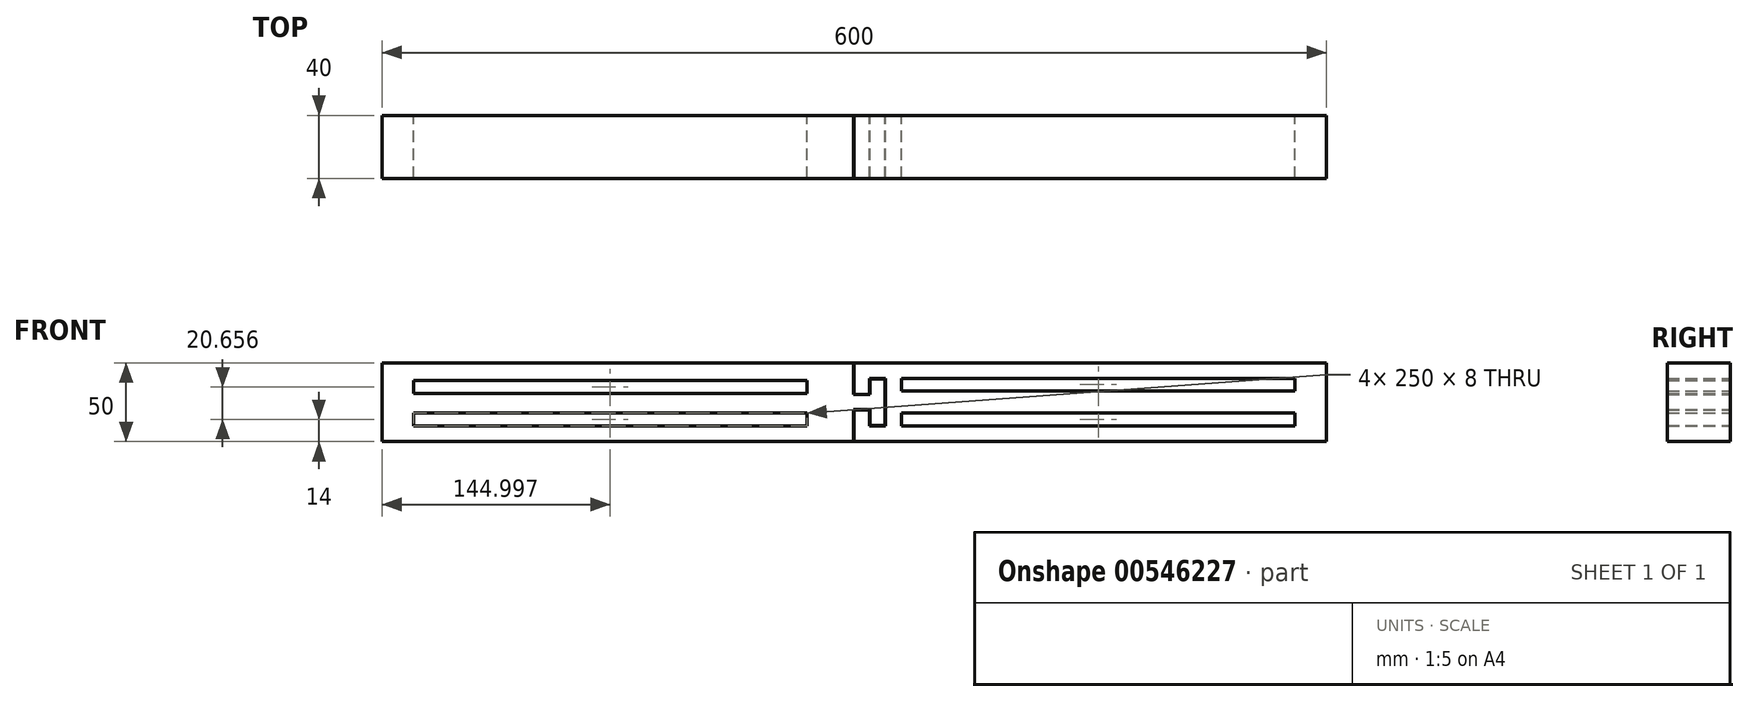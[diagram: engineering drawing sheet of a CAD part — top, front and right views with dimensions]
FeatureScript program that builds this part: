
annotation { "Feature Type Name" : "Feature", "Feature Type Description" : "" }
export const myFeature = defineFeature(function(context is Context, id is Id, definition is map)
    precondition{}
    {
        {
            var Q0;
            Q0=qCreatedBy(makeId("Front.planeOp"),FACE);
            var sketch = newSketch(context, id + "F0", { "sketchPlane" : qUnion([Q0])});
            skLineSegment(sketch, "E0.bottom", {"start": v(-57.6, 40) * mm, "end": v(542.4, 40) * mm});
            skLineSegment(sketch, "E0.top", {"start": v(-57.6, -10) * mm, "end": v(542.4, -10) * mm});
            skLineSegment(sketch, "E0.left", {"start": v(-57.6, 40) * mm, "end": v(-57.6, -10) * mm});
            skLineSegment(sketch, "E0.right", {"start": v(542.4, 40) * mm, "end": v(542.4, -10) * mm});
            skLineSegment(sketch, "E1", {"start": v(242.16, 40) * mm, "end": v(242.16, 20) * mm});
            skLineSegment(sketch, "E2.bottom", {"start": v(-37.6, 28.66) * mm, "end": v(212.4, 28.66) * mm});
            skLineSegment(sketch, "E2.top", {"start": v(-37.6, 20.66) * mm, "end": v(212.4, 20.66) * mm});
            skLineSegment(sketch, "E2.left", {"start": v(-37.6, 28.66) * mm, "end": v(-37.6, 20.66) * mm});
            skLineSegment(sketch, "E2.right", {"start": v(212.4, 28.66) * mm, "end": v(212.4, 20.66) * mm});
            skLineSegment(sketch, "E3.bottom", {"start": v(212.4, 8) * mm, "end": v(-37.6, 8) * mm});
            skLineSegment(sketch, "E3.top", {"start": v(212.4, 0) * mm, "end": v(-37.6, 0) * mm});
            skLineSegment(sketch, "E3.left", {"start": v(212.4, 8) * mm, "end": v(212.4, 0) * mm});
            skLineSegment(sketch, "E3.right", {"start": v(-37.6, 8) * mm, "end": v(-37.6, 0) * mm});
            skLineSegment(sketch, "E4.bottom", {"start": v(272.4, 30.16) * mm, "end": v(522.4, 30.16) * mm});
            skLineSegment(sketch, "E4.top", {"start": v(272.4, 22.16) * mm, "end": v(522.4, 22.16) * mm});
            skLineSegment(sketch, "E4.left", {"start": v(272.4, 30.16) * mm, "end": v(272.4, 22.16) * mm});
            skLineSegment(sketch, "E4.right", {"start": v(522.4, 30.16) * mm, "end": v(522.4, 22.16) * mm});
            skLineSegment(sketch, "E5.bottom", {"start": v(522.4, 8) * mm, "end": v(272.4, 8) * mm});
            skLineSegment(sketch, "E5.top", {"start": v(522.4, 0) * mm, "end": v(272.4, 0) * mm});
            skLineSegment(sketch, "E5.left", {"start": v(522.4, 8) * mm, "end": v(522.4, 0) * mm});
            skLineSegment(sketch, "E5.right", {"start": v(272.4, 8) * mm, "end": v(272.4, 0) * mm});
            skLineSegment(sketch, "E6", {"start": v(242.16, 20) * mm, "end": v(252.16, 20) * mm});
            skLineSegment(sketch, "E7", {"start": v(252.16, 20) * mm, "end": v(252.16, 30) * mm});
            skLineSegment(sketch, "E8", {"start": v(252.16, 30) * mm, "end": v(262.16, 30) * mm});
            skLineSegment(sketch, "E9", {"start": v(262.16, 30) * mm, "end": v(262.16, 0) * mm});
            skLineSegment(sketch, "E10", {"start": v(262.16, 0) * mm, "end": v(252.16, 0) * mm});
            skLineSegment(sketch, "E11", {"start": v(252.16, 0) * mm, "end": v(252.16, 10) * mm});
            skLineSegment(sketch, "E12", {"start": v(252.16, 10) * mm, "end": v(242.16, 10) * mm});
            skLineSegment(sketch, "E13.trimOffspring", {"start": v(242.16, 10) * mm, "end": v(242.16, -10) * mm});
            skLineSegment(sketch, "E14", {"start": v(242.16, 19.75) * mm, "end": v(252.4, 19.75) * mm});
            skLineSegment(sketch, "E15", {"start": v(252.4, 19.75) * mm, "end": v(252.4, 29.75) * mm});
            skLineSegment(sketch, "E16", {"start": v(252.4, 29.75) * mm, "end": v(261.9, 29.75) * mm});
            skLineSegment(sketch, "E17", {"start": v(261.9, 29.75) * mm, "end": v(261.9, 0.25) * mm});
            skLineSegment(sketch, "E18", {"start": v(261.9, 0.25) * mm, "end": v(252.4, 0.25) * mm});
            skLineSegment(sketch, "E19", {"start": v(252.4, 0.25) * mm, "end": v(252.4, 10.25) * mm});
            skLineSegment(sketch, "E20", {"start": v(252.4, 10.25) * mm, "end": v(242.16, 10.25) * mm});
            skLineSegment(sketch, "E21", {"start": v(241.9, 40) * mm, "end": v(241.9, 19.75) * mm});
            skLineSegment(sketch, "E22", {"start": v(242.16, 19.75) * mm, "end": v(241.9, 19.75) * mm});
            skLineSegment(sketch, "E23", {"start": v(242.16, 10.25) * mm, "end": v(241.9, 10.25) * mm});
            skLineSegment(sketch, "E24.trimOffspring", {"start": v(241.9, 10.25) * mm, "end": v(241.9, -10) * mm});
            skSolve(sketch);
        }
        {
            var Q0;
            {var subQ0=sQuery(id+"F0.wireOp",EDGE,"E0.right");Q0=makeQuery(id+"F0.imprint","IMPRINT",FACE,{"disambiguationData":[TD([[makeQuery(id+"F0.imprint","IMPRINT",EDGE,{"derivedFrom":subQ0}),-1.0]])]});}
            extrude(context, id + "F1", {"entities" : qUnion([Q0]), "depth" : 40 * mm, "offsetDistance" : 25 * mm});
        }
        {
            var Q0;
            {var subQ1=sQuery(id+"F0.wireOp",EDGE,"E0.left");Q0=makeQuery(id+"F0.imprint","IMPRINT",FACE,{"disambiguationData":[TD([[makeQuery(id+"F0.imprint","IMPRINT",EDGE,{"derivedFrom":subQ1}),1.0]])]});}
            extrude(context, id + "F2", {"entities" : qUnion([Q0]), "operationType" : NewBodyOperationType.ADD, "depth" : 40 * mm, "offsetDistance" : 25 * mm});
        }
    });
